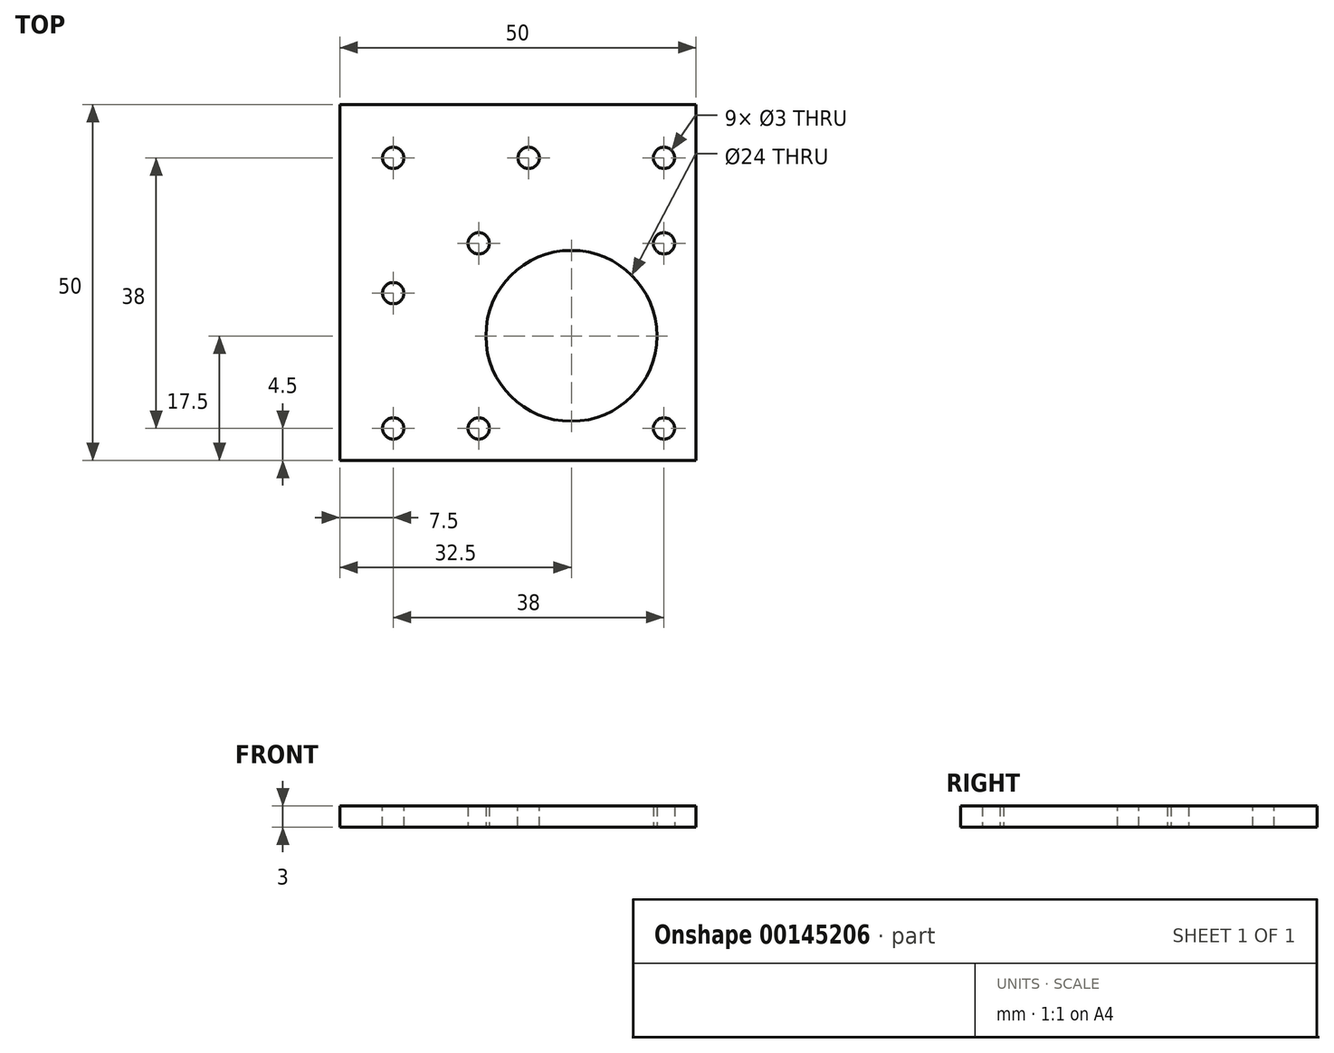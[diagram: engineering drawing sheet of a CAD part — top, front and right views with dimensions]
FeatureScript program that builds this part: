
annotation { "Feature Type Name" : "Feature", "Feature Type Description" : "" }
export const myFeature = defineFeature(function(context is Context, id is Id, definition is map)
    precondition{}
    {
        {
            var Q0;
            Q0=qCreatedBy(makeId("Top.planeOp"),FACE);
            var sketch = newSketch(context, id + "F0", { "sketchPlane" : qUnion([Q0])});
            skLineSegment(sketch, "E0.bottom", {"start": v(17.5, -17.5) * mm, "end": v(-17.5, -17.5) * mm});
            skLineSegment(sketch, "E0.top", {"start": v(17.5, 17.5) * mm, "end": v(-17.5, 17.5) * mm});
            skLineSegment(sketch, "E0.left", {"start": v(17.5, -17.5) * mm, "end": v(17.5, 17.5) * mm});
            skLineSegment(sketch, "E0.right", {"start": v(-17.5, -17.5) * mm, "end": v(-17.5, 17.5) * mm});
            skPoint(sketch, "E0.middle", {"position": v(0, 0) * mm});
            skCircle(sketch, "E1", {"center": v(0, 0) * mm, "radius": 12 * mm});
            skLineSegment(sketch, "E2", {"start": v(0, 0) * mm, "end": v(0, 13) * mm});
            skLineSegment(sketch, "E3", {"start": v(0, 13) * mm, "end": v(-13, 13) * mm});
            skCircle(sketch, "E4", {"center": v(-13, 13) * mm, "radius": 1.5 * mm});
            skCircle(sketch, "E5.1.0", {"center": v(-13, -13) * mm, "radius": 1.5 * mm});
            skCircle(sketch, "E5.2.0", {"center": v(13, -13) * mm, "radius": 1.5 * mm});
            skCircle(sketch, "E5.3.0", {"center": v(13, 13) * mm, "radius": 1.5 * mm});
            skSolve(sketch);
        }
        {
            var Q0;
            Q0=makeQuery(id+"F0.imprint","IMPRINT",FACE,{"disambiguationData":[TD([[makeQuery(id+"F0.imprint","IMPRINT",EDGE,{"derivedFrom":sQuery(id+"F0.wireOp",EDGE,"E0.bottom")}),-1.0]])]});
            extrude(context, id + "F1", {"entities" : qUnion([Q0]), "depth" : 3 * mm});
        }
        {
            var Q0;
            Q0=makeQuery(id+"F1.opExtrude","CAP_FACE",FACE,{"disambiguationData":[OSD([sQuery(id+"F0.wireOp",EDGE,"E0.bottom"),sQuery(id+"F0.wireOp",EDGE,"E0.top"),sQuery(id+"F0.wireOp",EDGE,"E0.left"),sQuery(id+"F0.wireOp",EDGE,"E0.right"),sQuery(id+"F0.wireOp",EDGE,"E1"),sQuery(id+"F0.wireOp",EDGE,"E4"),sQuery(id+"F0.wireOp",EDGE,"E5.1.0"),sQuery(id+"F0.wireOp",EDGE,"E5.2.0"),sQuery(id+"F0.wireOp",EDGE,"E5.3.0")])],"isStart":false});
            var sketch = newSketch(context, id + "F2", { "sketchPlane" : qUnion([Q0])});
            skLineSegment(sketch, "E6.0", {"start": v(17.5, 32.5) * mm, "end": v(-32.5, 32.5) * mm});
            skLineSegment(sketch, "E6.1", {"start": v(-32.5, -17.5) * mm, "end": v(-32.5, 32.5) * mm});
            skLineSegment(sketch, "E7", {"start": v(-32.5, -17.5) * mm, "end": v(-17.5, -17.5) * mm});
            skLineSegment(sketch, "E8", {"start": v(-17.5, -17.5) * mm, "end": v(-17.5, 17.5) * mm});
            skLineSegment(sketch, "E9", {"start": v(-17.5, 17.5) * mm, "end": v(17.5, 17.5) * mm});
            skLineSegment(sketch, "E10", {"start": v(17.5, 17.5) * mm, "end": v(17.5, 32.5) * mm});
            skSolve(sketch);
        }
        {
            var Q0;
            Q0=makeQuery(id+"F2.imprint","IMPRINT",FACE,{"disambiguationData":[TD([[makeQuery(id+"F2.imprint","IMPRINT",EDGE,{"derivedFrom":sQuery(id+"F2.wireOp",EDGE,"E6.0")}),1.0]])]});
            extrude(context, id + "F3", {"entities" : qUnion([Q0]), "operationType" : NewBodyOperationType.ADD, "oppositeDirection" : true, "depth" : 3 * mm});
        }
        {
            var Q0;
            Q0=makeQuery(id+"F3.boolean.opBoolean","MERGE",FACE,{"derivedFrom":[makeQuery(id+"F1.opExtrude","CAP_FACE",FACE,{"disambiguationData":[OSD([sQuery(id+"F0.wireOp",EDGE,"E0.bottom"),sQuery(id+"F0.wireOp",EDGE,"E0.top"),sQuery(id+"F0.wireOp",EDGE,"E0.left"),sQuery(id+"F0.wireOp",EDGE,"E0.right"),sQuery(id+"F0.wireOp",EDGE,"E1"),sQuery(id+"F0.wireOp",EDGE,"E4"),sQuery(id+"F0.wireOp",EDGE,"E5.1.0"),sQuery(id+"F0.wireOp",EDGE,"E5.2.0"),sQuery(id+"F0.wireOp",EDGE,"E5.3.0")])],"isStart":false}),makeQuery(id+"F3.opExtrude","CAP_FACE",FACE,{"disambiguationData":[OSD([sQuery(id+"F2.wireOp",EDGE,"E6.0"),sQuery(id+"F2.wireOp",EDGE,"E6.1"),sQuery(id+"F2.wireOp",EDGE,"E7"),sQuery(id+"F2.wireOp",EDGE,"E8"),sQuery(id+"F2.wireOp",EDGE,"E9"),sQuery(id+"F2.wireOp",EDGE,"E10")])],"isStart":true})]});
            var sketch = newSketch(context, id + "F4", { "sketchPlane" : qUnion([Q0])});
            skLineSegment(sketch, "E11.0", {"start": v(17.5, 25) * mm, "end": v(-25, 25) * mm});
            skLineSegment(sketch, "E11.1", {"start": v(-25, -17.5) * mm, "end": v(-25, 25) * mm});
            skCircle(sketch, "E12", {"center": v(-25, 25) * mm, "radius": 1.5 * mm});
            skLineSegment(sketch, "E13", {"start": v(-13, -13) * mm, "end": v(-25, -13) * mm});
            skCircle(sketch, "E14", {"center": v(-25, -13) * mm, "radius": 1.5 * mm});
            skLineSegment(sketch, "E15", {"start": v(13, 13) * mm, "end": v(13, 25) * mm});
            skCircle(sketch, "E16", {"center": v(13, 25) * mm, "radius": 1.5 * mm});
            skLineSegment(sketch, "E17", {"start": v(-25, 25) * mm, "end": v(13, 25) * mm});
            skCircle(sketch, "E18", {"center": v(-6, 25) * mm, "radius": 1.5 * mm});
            skLineSegment(sketch, "E19", {"start": v(-25, 25) * mm, "end": v(-25, -13) * mm});
            skCircle(sketch, "E20", {"center": v(-25, 6) * mm, "radius": 1.5 * mm});
            skSolve(sketch);
        }
        {
            var Q0;
            Q0 = qSketchRegion(id + "F4", true);
            extrude(context, id + "F5", {"entities" : qUnion([Q0]), "operationType" : NewBodyOperationType.REMOVE, "oppositeDirection" : true, "depth" : 25 * mm});
        }
    });
